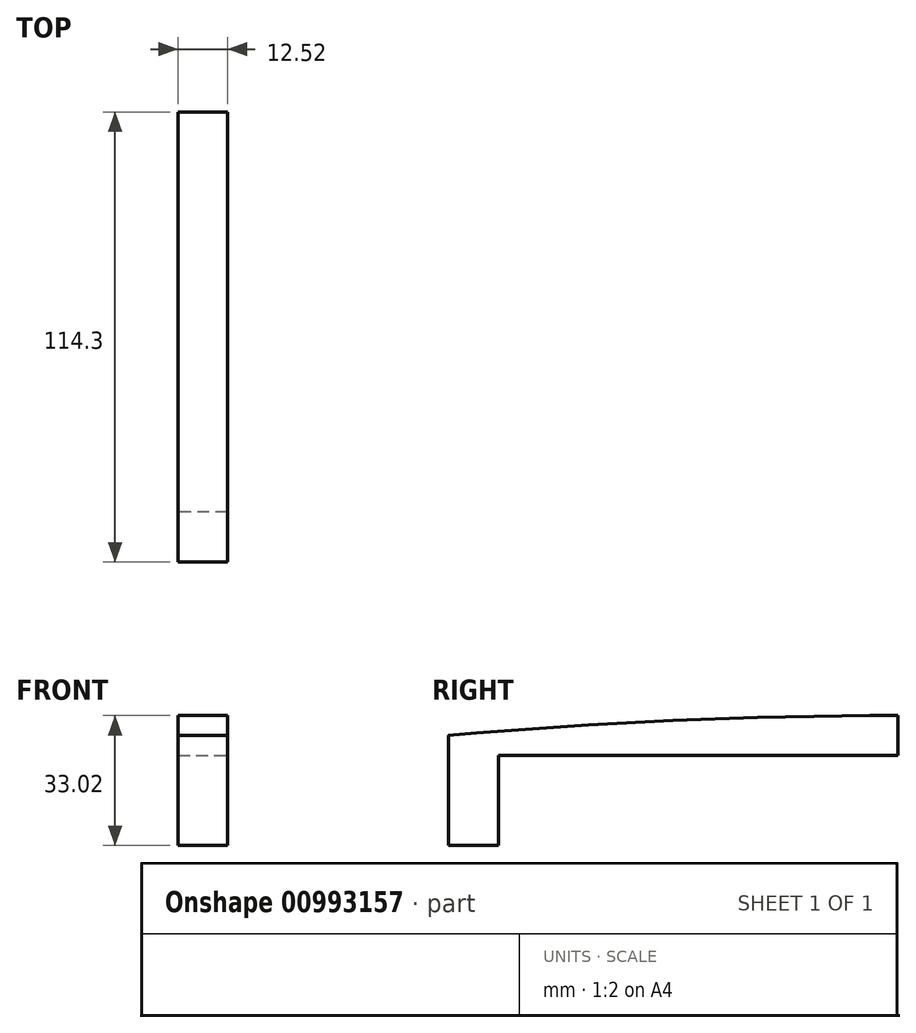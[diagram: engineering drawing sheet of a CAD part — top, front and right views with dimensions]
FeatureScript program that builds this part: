
annotation { "Feature Type Name" : "Feature", "Feature Type Description" : "" }
export const myFeature = defineFeature(function(context is Context, id is Id, definition is map)
    precondition{}
    {
        {
            var Q0;
            Q0=qCreatedBy(makeId("Top.planeOp"),FACE);
            var sketch = newSketch(context, id + "F0", { "sketchPlane" : qUnion([Q0])});
            skLineSegment(sketch, "E0.bottom", {"start": v(-50.16, 43.68) * mm, "end": v(-37.64, 43.68) * mm});
            skLineSegment(sketch, "E0.top", {"start": v(-50.16, -70.62) * mm, "end": v(-37.64, -70.62) * mm});
            skLineSegment(sketch, "E0.left", {"start": v(-50.16, 43.68) * mm, "end": v(-50.16, -70.62) * mm});
            skLineSegment(sketch, "E0.right", {"start": v(-37.64, 43.68) * mm, "end": v(-37.64, -70.62) * mm});
            skSolve(sketch);
        }
        {
            var Q0;
            Q0=makeQuery(id+"F0.imprint","IMPRINT",FACE,{"disambiguationData":[TD([[makeQuery(id+"F0.imprint","IMPRINT",EDGE,{"derivedFrom":sQuery(id+"F0.wireOp",EDGE,"E0.bottom")}),-1.0]])]});
            extrude(context, id + "F1", {"entities" : qUnion([Q0]), "depth" : 10.16 * mm, "offsetDistance" : 25.4 * mm});
        }
        {
            var Q0;
            Q0=makeQuery(id+"F1.opExtrude","SWEPT_FACE",FACE,{"disambiguationData":[OSD([sQuery(id+"F0.wireOp",EDGE,"E0.right")])]});
            var sketch = newSketch(context, id + "F2", { "sketchPlane" : qUnion([Q0])});
            skArc(sketch, "E1", {"start": v(43.68, 10.16) * mm, "mid": v(-13.52, 8.89) * mm, "end": v(-70.62, 5.08) * mm});
            skSolve(sketch);
        }
        {
            var Q0;
            {var subQ0=sQuery(id+"F2.wireOp",EDGE,"E1");Q0=makeQuery(id+"F2.imprint","IMPRINT",FACE,{"disambiguationData":[TD([[makeQuery(id+"F2.imprint","IMPRINT",EDGE,{"derivedFrom":subQ0}),-1.0]])]});}
            extrude(context, id + "F3", {"entities" : qUnion([Q0]), "operationType" : NewBodyOperationType.REMOVE, "oppositeDirection" : true, "depth" : 25.4 * mm, "offsetDistance" : 25.4 * mm});
        }
        {
            var Q0;
            Q0=makeQuery(id+"F1.opExtrude","CAP_FACE",FACE,{"disambiguationData":[OSD([sQuery(id+"F0.wireOp",EDGE,"E0.bottom"),sQuery(id+"F0.wireOp",EDGE,"E0.top"),sQuery(id+"F0.wireOp",EDGE,"E0.left"),sQuery(id+"F0.wireOp",EDGE,"E0.right")])],"isStart":true});
            var sketch = newSketch(context, id + "F4", { "sketchPlane" : qUnion([Q0])});
            skLineSegment(sketch, "E2", {"start": v(-37.64, 57.92) * mm, "end": v(-50.16, 57.92) * mm});
            skSolve(sketch);
        }
        {
            var Q0;
            {var subQ0=sQuery(id+"F4.wireOp",EDGE,"E2");Q0=makeQuery(id+"F4.imprint","IMPRINT",FACE,{"disambiguationData":[TD([[makeQuery(id+"F4.imprint","IMPRINT",EDGE,{"derivedFrom":subQ0}),-1.0]])]});}
            extrude(context, id + "F5", {"entities" : qUnion([Q0]), "operationType" : NewBodyOperationType.ADD, "depth" : 22.86 * mm, "offsetDistance" : 25.4 * mm});
        }
    });
